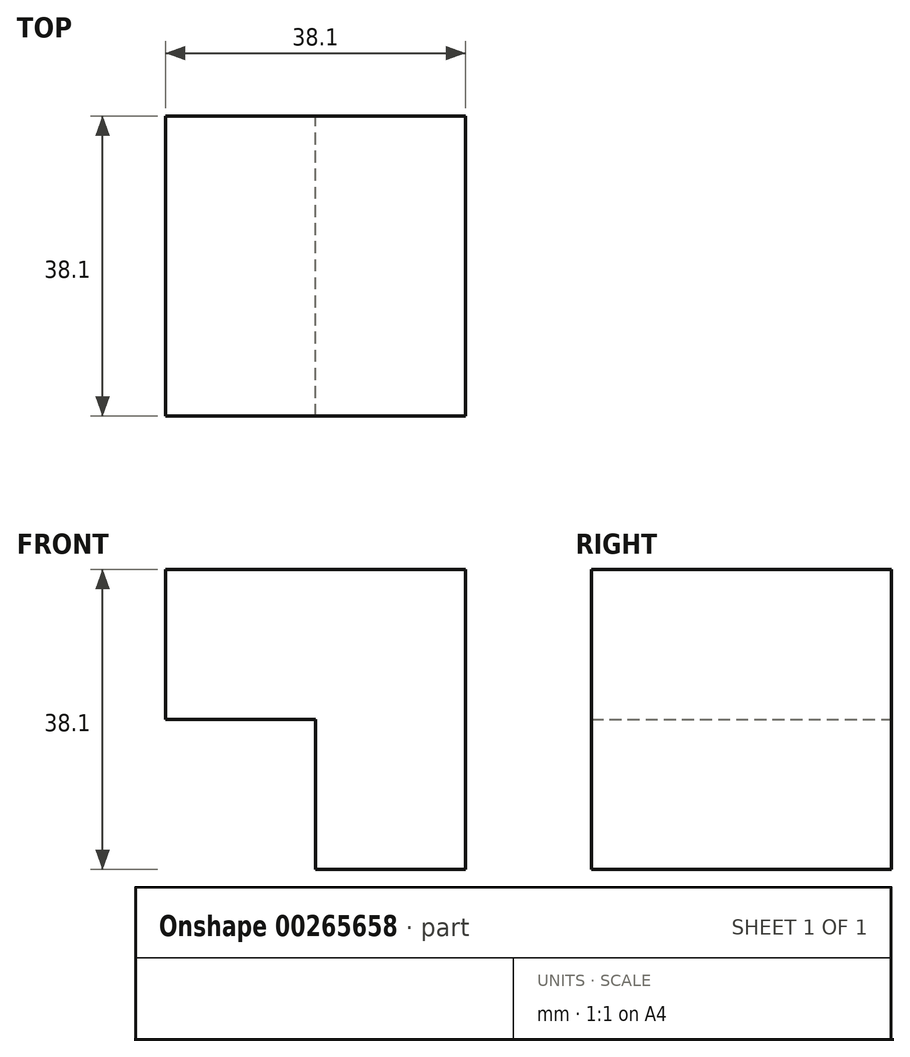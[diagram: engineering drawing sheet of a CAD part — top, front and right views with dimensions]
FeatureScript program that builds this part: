
annotation { "Feature Type Name" : "Feature", "Feature Type Description" : "" }
export const myFeature = defineFeature(function(context is Context, id is Id, definition is map)
    precondition{}
    {
        {
            var Q0;
            Q0=qCreatedBy(makeId("Front.planeOp"),FACE);
            var sketch = newSketch(context, id + "F0", { "sketchPlane" : qUnion([Q0])});
            skLineSegment(sketch, "E0.bottom", {"start": v(-48.62, 35.85) * mm, "end": v(-29.57, 35.85) * mm});
            skLineSegment(sketch, "E0.top", {"start": v(-48.62, 16.8) * mm, "end": v(-29.57, 16.8) * mm});
            skLineSegment(sketch, "E0.left", {"start": v(-48.62, 35.85) * mm, "end": v(-48.62, 16.8) * mm});
            skLineSegment(sketch, "E0.right", {"start": v(-29.57, 35.85) * mm, "end": v(-29.57, 16.8) * mm});
            skLineSegment(sketch, "E1.MirrorCS", {"start": v(-48.62, 16.8) * mm, "end": v(-67.67, 16.8) * mm});
            skLineSegment(sketch, "E2.MirrorCS", {"start": v(-48.62, 35.85) * mm, "end": v(-67.67, 35.85) * mm});
            skLineSegment(sketch, "E3.MirrorCS", {"start": v(-67.67, 35.85) * mm, "end": v(-67.67, 16.8) * mm});
            skLineSegment(sketch, "E4.MirrorCS", {"start": v(-48.62, -2.25) * mm, "end": v(-48.62, 16.8) * mm});
            skLineSegment(sketch, "E5.MirrorCS", {"start": v(-29.57, -2.25) * mm, "end": v(-29.57, 16.8) * mm});
            skLineSegment(sketch, "E6.MirrorCS", {"start": v(-48.62, -2.25) * mm, "end": v(-29.57, -2.25) * mm});
            skSolve(sketch);
        }
        {
            var Q0;
            Q0 = qSketchRegion(id + "F0", true);
            extrude(context, id + "F1", {"entities" : qUnion([Q0]), "depth" : 38.1 * mm});
        }
    });
